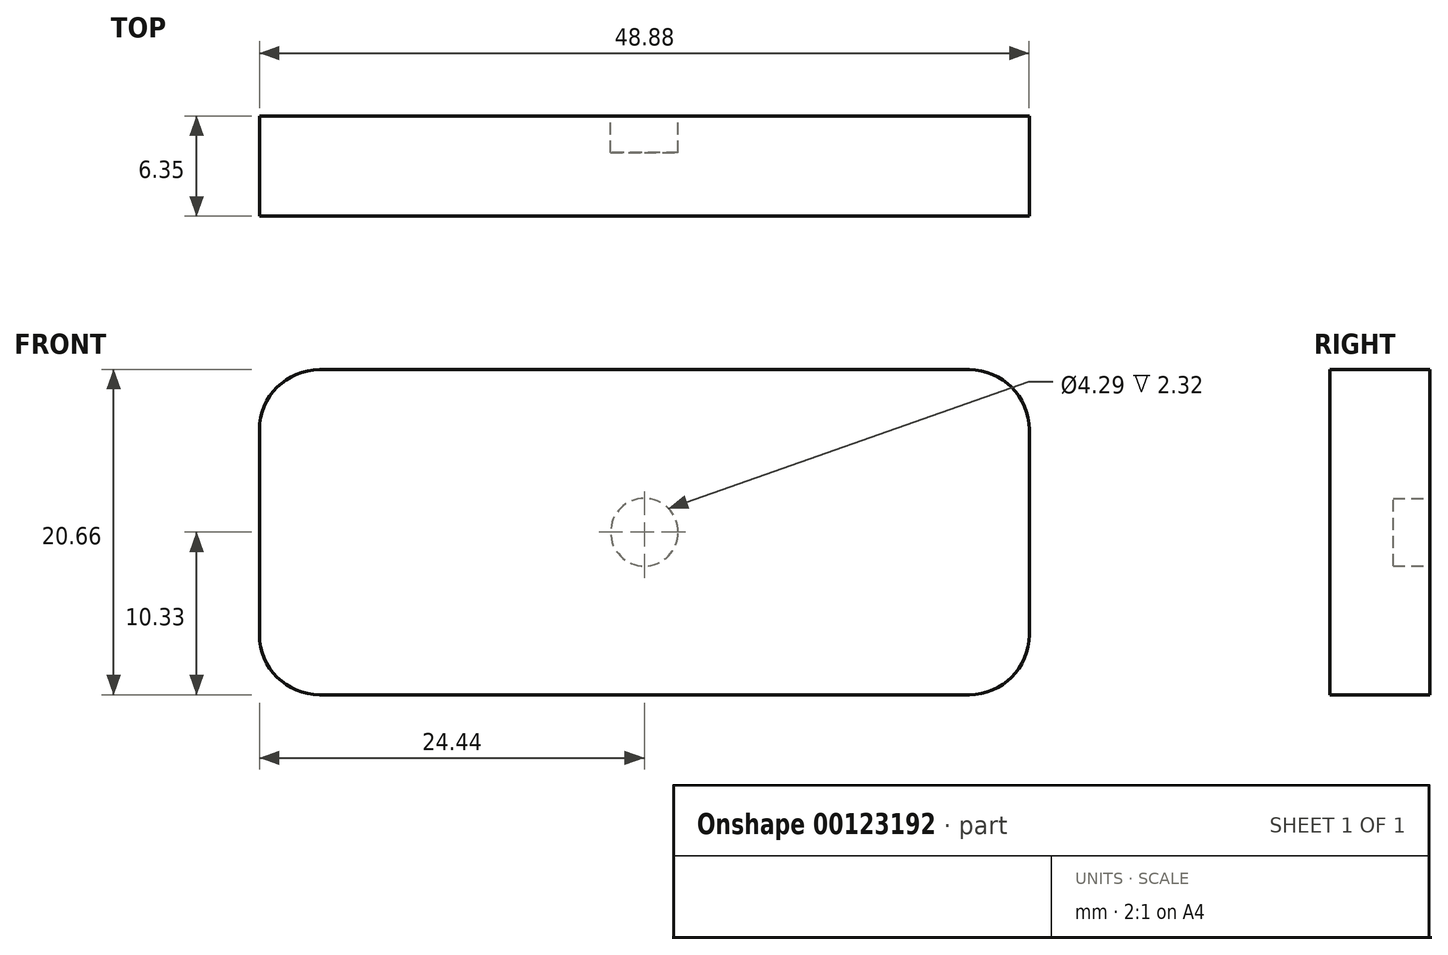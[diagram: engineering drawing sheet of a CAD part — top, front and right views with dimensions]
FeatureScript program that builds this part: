
annotation { "Feature Type Name" : "Feature", "Feature Type Description" : "" }
export const myFeature = defineFeature(function(context is Context, id is Id, definition is map)
    precondition{}
    {
        {
            var Q0;
            Q0=qCreatedBy(makeId("Front.planeOp"),FACE);
            var sketch = newSketch(context, id + "F0", { "sketchPlane" : qUnion([Q0])});
            skLineSegment(sketch, "E0.bottom", {"start": v(-20.63, 10.33) * mm, "end": v(20.63, 10.33) * mm});
            skLineSegment(sketch, "E0.top", {"start": v(-20.63, -10.33) * mm, "end": v(20.63, -10.33) * mm});
            skLineSegment(sketch, "E0.left", {"start": v(-24.44, 6.52) * mm, "end": v(-24.44, -6.52) * mm});
            skLineSegment(sketch, "E0.right", {"start": v(24.44, 6.52) * mm, "end": v(24.44, -6.52) * mm});
            skPoint(sketch, "E0.middle", {"position": v(0, 0) * mm});
            skPoint(sketch, "E1.visualSharp", {"position": v(24.44, -10.33) * mm});
            skArc(sketch, "E1.filletArc", {"start": v(20.63, -10.33) * mm, "mid": v(23.33, -9.2) * mm, "end": v(24.44, -6.52) * mm});
            skPoint(sketch, "E2.visualSharp", {"position": v(24.44, 10.33) * mm});
            skArc(sketch, "E2.filletArc", {"start": v(24.44, 6.52) * mm, "mid": v(23.33, 9.2) * mm, "end": v(20.63, 10.33) * mm});
            skPoint(sketch, "E3.visualSharp", {"position": v(-24.44, 10.33) * mm});
            skArc(sketch, "E3.filletArc", {"start": v(-20.63, 10.33) * mm, "mid": v(-23.33, 9.2) * mm, "end": v(-24.44, 6.52) * mm});
            skPoint(sketch, "E4.visualSharp", {"position": v(-24.44, -10.33) * mm});
            skArc(sketch, "E4.filletArc", {"start": v(-24.44, -6.52) * mm, "mid": v(-23.33, -9.2) * mm, "end": v(-20.63, -10.33) * mm});
            skSolve(sketch);
        }
        {
            var Q0;
            Q0 = qSketchRegion(id + "F0", true);
            extrude(context, id + "F1", {"entities" : qUnion([Q0]), "depth" : 6.35 * mm});
        }
        {
            var Q0;
            Q0=qCreatedBy(makeId("Front.planeOp"),FACE);
            var sketch = newSketch(context, id + "F2", { "sketchPlane" : qUnion([Q0])});
            skCircle(sketch, "E5", {"center": v(0, 0) * mm, "radius": 2.15 * mm});
            skSolve(sketch);
        }
        {
            var Q0;
            Q0=makeQuery(id+"F2.imprint","IMPRINT",FACE,{"disambiguationData":[TD([[makeQuery(id+"F2.imprint","IMPRINT",EDGE,{"derivedFrom":sQuery(id+"F2.wireOp",EDGE,"E5")}),1.0]])]});
            extrude(context, id + "F3", {"entities" : qUnion([Q0]), "operationType" : NewBodyOperationType.REMOVE, "depth" : 2.32 * mm});
        }
    });
